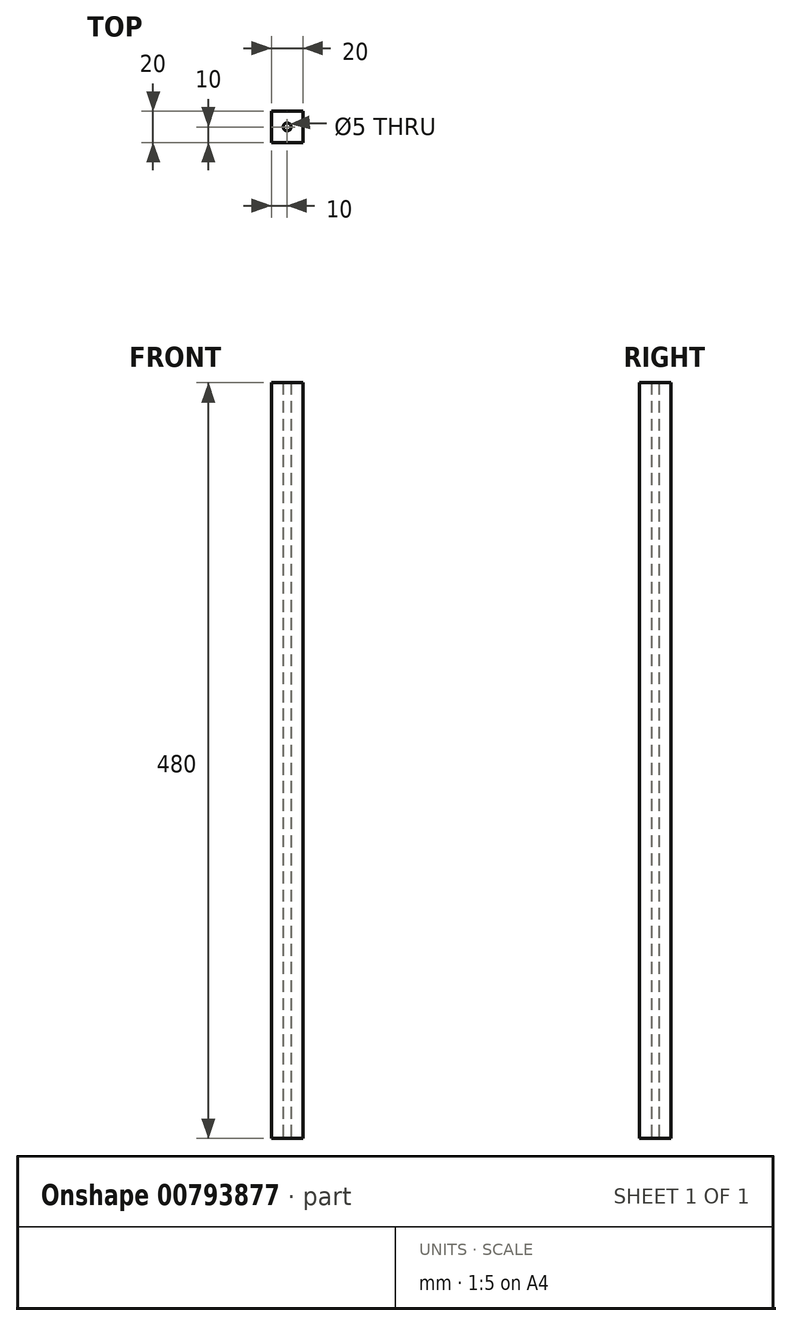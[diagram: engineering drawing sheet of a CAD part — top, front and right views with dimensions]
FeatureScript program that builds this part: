
annotation { "Feature Type Name" : "Feature", "Feature Type Description" : "" }
export const myFeature = defineFeature(function(context is Context, id is Id, definition is map)
    precondition{}
    {
        {
            var Q0;
            Q0=qCreatedBy(makeId("Top.planeOp"),FACE);
            var sketch = newSketch(context, id + "F0", { "sketchPlane" : qUnion([Q0])});
            skLineSegment(sketch, "E0.bottom", {"start": v(-10, 10) * mm, "end": v(10, 10) * mm});
            skLineSegment(sketch, "E0.top", {"start": v(-10, -10) * mm, "end": v(10, -10) * mm});
            skLineSegment(sketch, "E0.left", {"start": v(-10, 10) * mm, "end": v(-10, -10) * mm});
            skLineSegment(sketch, "E0.right", {"start": v(10, 10) * mm, "end": v(10, -10) * mm});
            skCircle(sketch, "E1", {"center": v(0, 0) * mm, "radius": 2.5 * mm});
            skSolve(sketch);
        }
        {
            var Q0;
            Q0=qSketchRegion(id+"F0",true);
            extrude(context, id + "F1", {"entities" : qUnion([Q0]), "depth" : 480 * mm, "offsetDistance" : 25 * mm});
        }
    });
